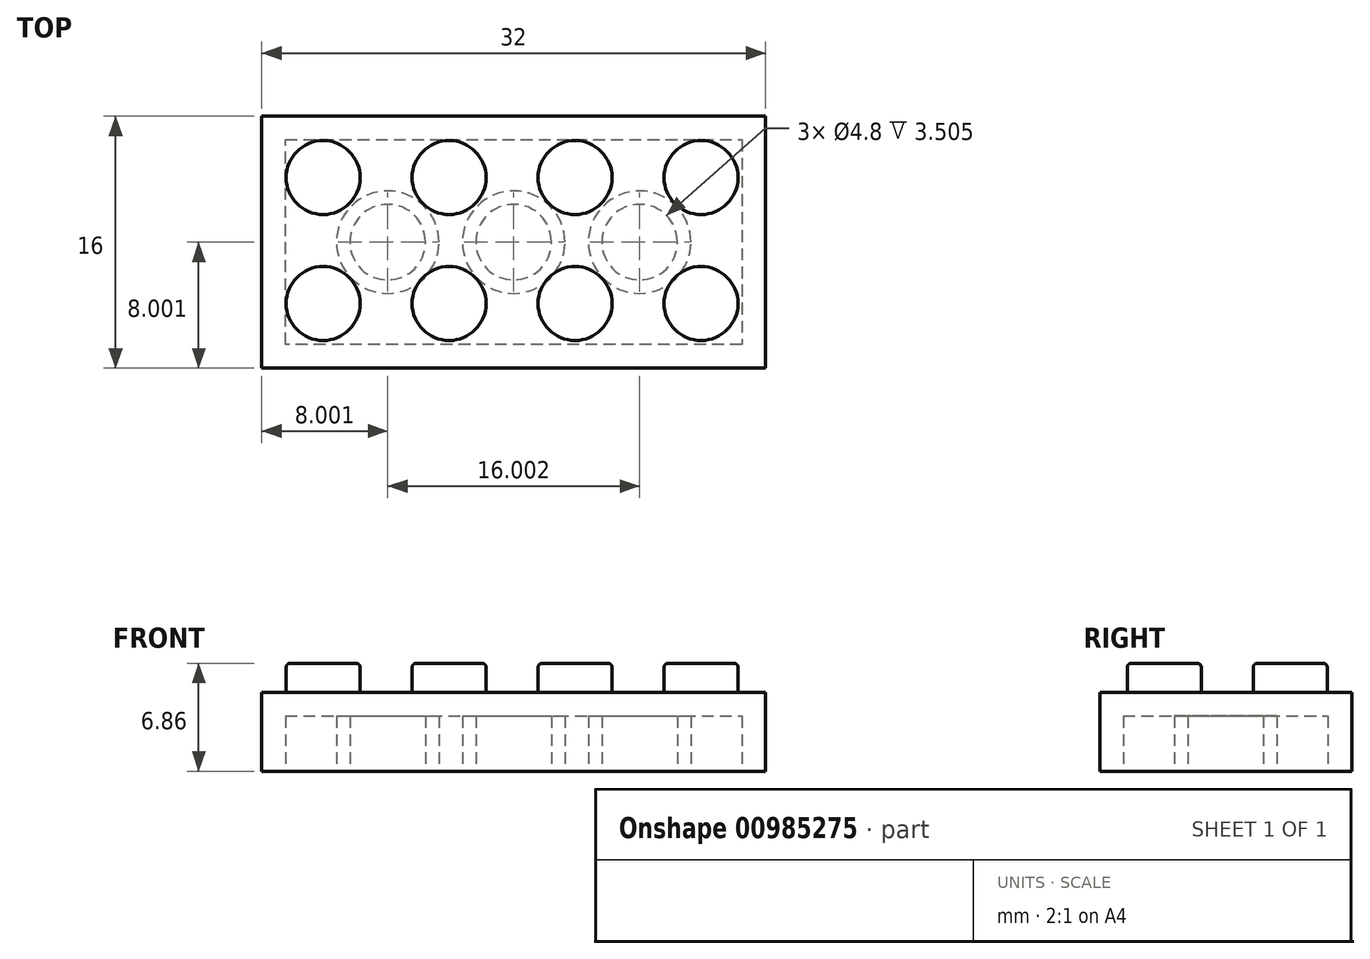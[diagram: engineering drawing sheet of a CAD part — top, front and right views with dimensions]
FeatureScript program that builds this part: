
annotation { "Feature Type Name" : "Feature", "Feature Type Description" : "" }
export const myFeature = defineFeature(function(context is Context, id is Id, definition is map)
    precondition{}
    {
        {
            var Q0;
            Q0=qCreatedBy(makeId("Top.planeOp"),FACE);
            var sketch = newSketch(context, id + "F0", { "sketchPlane" : qUnion([Q0])});
            skLineSegment(sketch, "E0.bottom", {"start": v(0, 0) * mm, "end": v(32, 0) * mm});
            skLineSegment(sketch, "E0.top", {"start": v(0, 16) * mm, "end": v(32, 16) * mm});
            skLineSegment(sketch, "E0.left", {"start": v(0, 0) * mm, "end": v(0, 16) * mm});
            skLineSegment(sketch, "E0.right", {"start": v(32, 0) * mm, "end": v(32, 16) * mm});
            skSolve(sketch);
        }
        {
            var Q0;
            Q0=makeQuery(id+"F0.imprint","IMPRINT",FACE,{"disambiguationData":[TD([[makeQuery(id+"F0.imprint","IMPRINT",EDGE,{"derivedFrom":sQuery(id+"F0.wireOp",EDGE,"E0.bottom")}),1.0]])]});
            extrude(context, id + "F1", {"entities" : qUnion([Q0]), "depth" : 5 * mm, "offsetDistance" : 25.4 * mm});
        }
        {
            var Q0;
            Q0=makeQuery(id+"F1.opExtrude","CAP_FACE",FACE,{"disambiguationData":[OSD([sQuery(id+"F0.wireOp",EDGE,"E0.bottom"),sQuery(id+"F0.wireOp",EDGE,"E0.top"),sQuery(id+"F0.wireOp",EDGE,"E0.left"),sQuery(id+"F0.wireOp",EDGE,"E0.right")])],"isStart":false});
            var sketch = newSketch(context, id + "F2", { "sketchPlane" : qUnion([Q0])});
            skCircle(sketch, "E1", {"center": v(3.9, 12.1) * mm, "radius": 2.35 * mm});
            skCircle(sketch, "E2.0.1.0", {"center": v(3.9, 4.1) * mm, "radius": 2.35 * mm});
            skCircle(sketch, "E2.1.0.0", {"center": v(11.9, 12.1) * mm, "radius": 2.35 * mm});
            skCircle(sketch, "E2.1.1.0", {"center": v(11.9, 4.1) * mm, "radius": 2.35 * mm});
            skCircle(sketch, "E2.2.0.0", {"center": v(19.9, 12.1) * mm, "radius": 2.35 * mm});
            skCircle(sketch, "E2.2.1.0", {"center": v(19.9, 4.1) * mm, "radius": 2.35 * mm});
            skCircle(sketch, "E2.3.0.0", {"center": v(27.9, 12.1) * mm, "radius": 2.35 * mm});
            skCircle(sketch, "E2.3.1.0", {"center": v(27.9, 4.1) * mm, "radius": 2.35 * mm});
            skLineSegment(sketch, "E2.direction1", {"start": v(3.9, 12.1) * mm, "end": v(11.9, 12.1) * mm, "construction": true});
            skLineSegment(sketch, "E2.direction2", {"start": v(3.9, 12.1) * mm, "end": v(3.9, 4.1) * mm, "construction": true});
            skSolve(sketch);
        }
        {
            var Q0;
            Q0=makeQuery(id+"F2.imprint","IMPRINT",FACE,{"disambiguationData":[TD([[makeQuery(id+"F2.imprint","IMPRINT",EDGE,{"derivedFrom":sQuery(id+"F2.wireOp",EDGE,"E2.0.1.0")}),1.0]])]});
            var Q1;
            Q1=makeQuery(id+"F2.imprint","IMPRINT",FACE,{"disambiguationData":[TD([[makeQuery(id+"F2.imprint","IMPRINT",EDGE,{"derivedFrom":sQuery(id+"F2.wireOp",EDGE,"E2.1.1.0")}),1.0]])]});
            var Q2;
            Q2=makeQuery(id+"F2.imprint","IMPRINT",FACE,{"disambiguationData":[TD([[makeQuery(id+"F2.imprint","IMPRINT",EDGE,{"derivedFrom":sQuery(id+"F2.wireOp",EDGE,"E2.2.1.0")}),1.0]])]});
            var Q3;
            Q3=makeQuery(id+"F2.imprint","IMPRINT",FACE,{"disambiguationData":[TD([[makeQuery(id+"F2.imprint","IMPRINT",EDGE,{"derivedFrom":sQuery(id+"F2.wireOp",EDGE,"E2.3.1.0")}),1.0]])]});
            var Q4;
            Q4=makeQuery(id+"F2.imprint","IMPRINT",FACE,{"disambiguationData":[TD([[makeQuery(id+"F2.imprint","IMPRINT",EDGE,{"derivedFrom":sQuery(id+"F2.wireOp",EDGE,"E2.2.0.0")}),1.0]])]});
            var Q5;
            Q5=makeQuery(id+"F2.imprint","IMPRINT",FACE,{"disambiguationData":[TD([[makeQuery(id+"F2.imprint","IMPRINT",EDGE,{"derivedFrom":sQuery(id+"F2.wireOp",EDGE,"E2.1.0.0")}),1.0]])]});
            var Q6;
            Q6=makeQuery(id+"F2.imprint","IMPRINT",FACE,{"disambiguationData":[TD([[makeQuery(id+"F2.imprint","IMPRINT",EDGE,{"derivedFrom":sQuery(id+"F2.wireOp",EDGE,"E1")}),1.0]])]});
            var Q7;
            Q7=makeQuery(id+"F2.imprint","IMPRINT",FACE,{"disambiguationData":[TD([[makeQuery(id+"F2.imprint","IMPRINT",EDGE,{"derivedFrom":sQuery(id+"F2.wireOp",EDGE,"E2.3.0.0")}),1.0]])]});
            extrude(context, id + "F3", {"entities" : qUnion([Q0, Q1, Q2, Q3, Q4, Q5, Q6, Q7]), "operationType" : NewBodyOperationType.ADD, "depth" : 1.85 * mm, "offsetDistance" : 25.4 * mm});
        }
        {
            var Q0;
            Q0=makeQuery(id+"F3.opExtrude","CAP_EDGE",EDGE,{"disambiguationData":[OSD([sQuery(id+"F2.wireOp",EDGE,"E2.1.0.0")])],"isStart":false});
            var Q1;
            Q1=makeQuery(id+"F3.opExtrude","CAP_EDGE",EDGE,{"disambiguationData":[OSD([sQuery(id+"F2.wireOp",EDGE,"E2.2.0.0")])],"isStart":false});
            var Q2;
            Q2=makeQuery(id+"F3.opExtrude","CAP_EDGE",EDGE,{"disambiguationData":[OSD([sQuery(id+"F2.wireOp",EDGE,"E2.3.0.0")])],"isStart":false});
            var Q3;
            Q3=makeQuery(id+"F3.opExtrude","CAP_FACE",FACE,{"disambiguationData":[OSD([sQuery(id+"F2.wireOp",EDGE,"E2.3.1.0")])],"isStart":false});
            var Q4;
            Q4=makeQuery(id+"F3.opExtrude","CAP_EDGE",EDGE,{"disambiguationData":[OSD([sQuery(id+"F2.wireOp",EDGE,"E2.2.1.0")])],"isStart":false});
            var Q5;
            Q5=makeQuery(id+"F3.opExtrude","CAP_EDGE",EDGE,{"disambiguationData":[OSD([sQuery(id+"F2.wireOp",EDGE,"E2.1.1.0")])],"isStart":false});
            var Q6;
            Q6=makeQuery(id+"F3.opExtrude","CAP_EDGE",EDGE,{"disambiguationData":[OSD([sQuery(id+"F2.wireOp",EDGE,"E2.0.1.0")])],"isStart":false});
            var Q7;
            Q7=makeQuery(id+"F3.opExtrude","CAP_FACE",FACE,{"disambiguationData":[OSD([sQuery(id+"F2.wireOp",EDGE,"E1")])],"isStart":false});
            fillet(context, id + "F4", {"entities" : qUnion([Q0, Q1, Q2, Q3, Q4, Q5, Q6, Q7]), "radius" : 0.25 * mm, "tangentPropagation" : true, "allowEdgeOverflow" : false});
        }
        {
            var Q0;
            Q0=makeQuery(id+"F1.opExtrude","CAP_FACE",FACE,{"disambiguationData":[OSD([sQuery(id+"F0.wireOp",EDGE,"E0.bottom"),sQuery(id+"F0.wireOp",EDGE,"E0.top"),sQuery(id+"F0.wireOp",EDGE,"E0.left"),sQuery(id+"F0.wireOp",EDGE,"E0.right")])],"isStart":true});
            var sketch = newSketch(context, id + "F5", { "sketchPlane" : qUnion([Q0])});
            skLineSegment(sketch, "E3.0", {"start": v(1.5, -14.5) * mm, "end": v(30.5, -14.5) * mm});
            skLineSegment(sketch, "E3.1", {"start": v(1.5, -1.5) * mm, "end": v(1.5, -14.5) * mm});
            skLineSegment(sketch, "E3.2", {"start": v(30.5, -1.5) * mm, "end": v(1.5, -1.5) * mm});
            skLineSegment(sketch, "E3.3", {"start": v(30.5, -14.5) * mm, "end": v(30.5, -1.5) * mm});
            skLineSegment(sketch, "E4", {"start": v(0, 0) * mm, "end": v(32, -16) * mm, "construction": true});
            skLineSegment(sketch, "E5", {"start": v(0, -16) * mm, "end": v(32, 0) * mm, "construction": true});
            skCircle(sketch, "E6", {"center": v(16, -8) * mm, "radius": 3.25 * mm});
            skCircle(sketch, "E7", {"center": v(16, -8) * mm, "radius": 2.4 * mm});
            skCircle(sketch, "E8", {"center": v(8, -8) * mm, "radius": 3.25 * mm});
            skCircle(sketch, "E9", {"center": v(8, -8) * mm, "radius": 2.4 * mm});
            skCircle(sketch, "E10", {"center": v(24, -8) * mm, "radius": 2.4 * mm});
            skCircle(sketch, "E11", {"center": v(24, -8) * mm, "radius": 3.25 * mm});
            skSolve(sketch);
        }
        {
            var Q0;
            Q0=makeQuery(id+"F5.imprint","IMPRINT",FACE,{"disambiguationData":[TD([[makeQuery(id+"F5.imprint","IMPRINT",EDGE,{"derivedFrom":sQuery(id+"F5.wireOp",EDGE,"E7")}),1.0]])]});
            var Q1;
            Q1=makeQuery(id+"F5.imprint","IMPRINT",FACE,{"disambiguationData":[TD([[makeQuery(id+"F5.imprint","IMPRINT",EDGE,{"derivedFrom":sQuery(id+"F5.wireOp",EDGE,"E9")}),1.0]])]});
            var Q2;
            Q2=makeQuery(id+"F5.imprint","IMPRINT",FACE,{"disambiguationData":[TD([[makeQuery(id+"F5.imprint","IMPRINT",EDGE,{"derivedFrom":sQuery(id+"F5.wireOp",EDGE,"E10")}),1.0]])]});
            var Q3;
            Q3=makeQuery(id+"F5.imprint","IMPRINT",FACE,{"disambiguationData":[TD([[makeQuery(id+"F5.imprint","IMPRINT",EDGE,{"derivedFrom":sQuery(id+"F5.wireOp",EDGE,"E3.0")}),1.0]])]});
            extrude(context, id + "F6", {"entities" : qUnion([Q0, Q1, Q2, Q3]), "operationType" : NewBodyOperationType.REMOVE, "oppositeDirection" : true, "depth" : 3.5 * mm, "offsetDistance" : 25.4 * mm});
        }
    });
